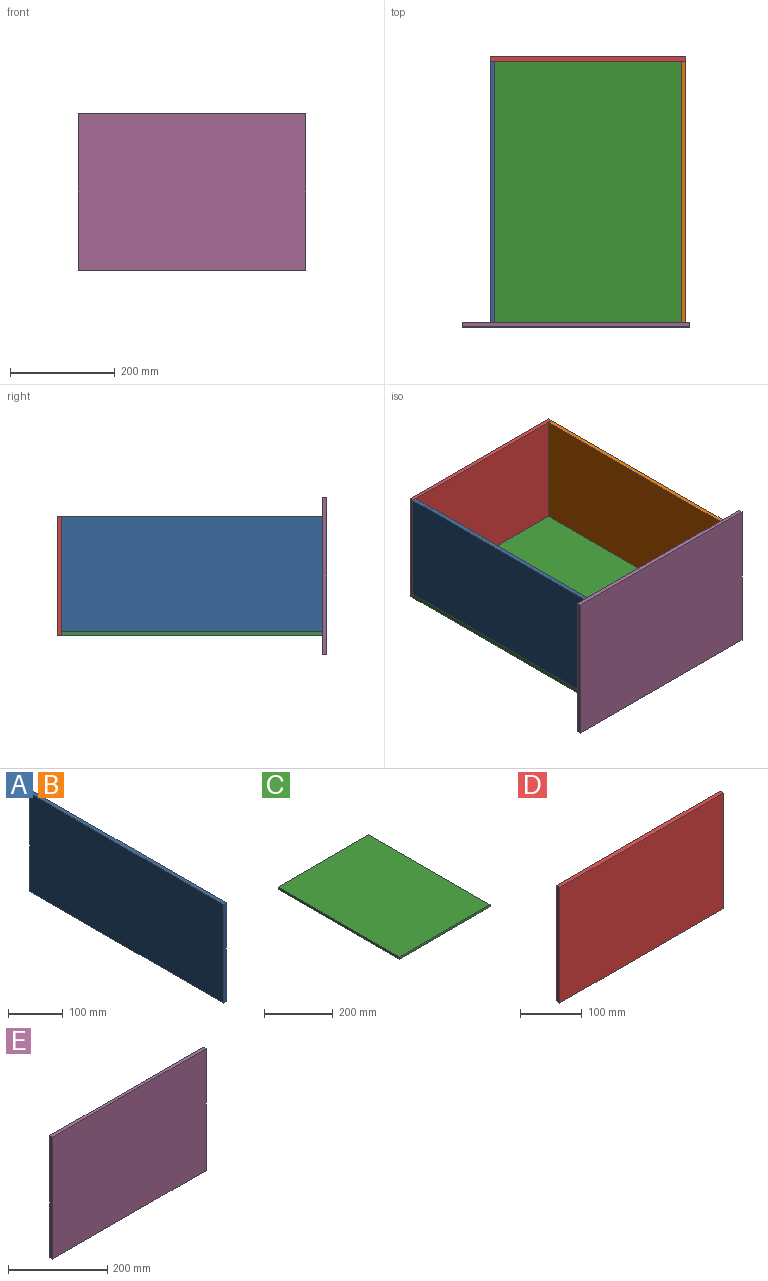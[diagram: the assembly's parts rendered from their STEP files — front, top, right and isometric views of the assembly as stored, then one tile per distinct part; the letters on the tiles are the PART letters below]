
ASSEMBLY  parts=5 mates=4
PART A: 6 faces, bbox 8x500x220 mm
  f0: plane 220x8mm, normal (0,1,0), area 1760mm2, adj f1,f3,f4,f5
  f1: plane 500x8mm, normal (0,0,1), area 4000mm2, adj f0,f2,f4,f5
  f2: plane 220x8mm, normal (0,-1,0), area 1760mm2, adj f1,f3,f4,f5
  f3: plane 500x8mm, normal (0,0,-1), area 4000mm2, adj f0,f2,f4,f5
  f4: plane 500x220mm, normal (1,0,0), area 110000mm2, adj f0,f1,f2,f3
  f5: plane 500x220mm, normal (-1,0,0), area 110000mm2, adj f0,f1,f2,f3
PART B: same geometry as A
PART C: 6 faces, bbox 374x500x8 mm
  f0: plane 500x8mm, normal (1,0,0), area 4000mm2, adj f1,f3,f4,f5
  f1: plane 374x8mm, normal (0,1,0), area 2992mm2, adj f0,f2,f4,f5
  f2: plane 500x8mm, normal (-1,0,0), area 4000mm2, adj f1,f3,f4,f5
  f3: plane 374x8mm, normal (0,-1,0), area 2992mm2, adj f0,f2,f4,f5
  f4: plane 500x374mm, normal (0,0,1), area 187000mm2, adj f0,f1,f2,f3
  f5: plane 500x374mm, normal (0,0,-1), area 187000mm2, adj f0,f1,f2,f3
PART D: 6 faces, bbox 374x8x228 mm
  f0: plane 228x8mm, normal (1,0,0), area 1824mm2, adj f1,f3,f4,f5
  f1: plane 374x8mm, normal (0,0,1), area 2992mm2, adj f0,f2,f4,f5
  f2: plane 228x8mm, normal (-1,0,0), area 1824mm2, adj f1,f3,f4,f5
  f3: plane 374x8mm, normal (0,0,-1), area 2992mm2, adj f0,f2,f4,f5
  f4: plane 374x228mm, normal (0,-1,0), area 85272mm2, adj f0,f1,f2,f3
  f5: plane 374x228mm, normal (0,1,0), area 85272mm2, adj f0,f1,f2,f3
PART E: 6 faces, bbox 436x8x300 mm
  f0: plane 300x8mm, normal (1,0,0), area 2400mm2, adj f1,f3,f4,f5
  f1: plane 436x8mm, normal (0,0,1), area 3488mm2, adj f0,f2,f4,f5
  f2: plane 300x8mm, normal (-1,0,0), area 2400mm2, adj f1,f3,f4,f5
  f3: plane 436x8mm, normal (0,0,-1), area 3488mm2, adj f0,f2,f4,f5
  f4: plane 436x300mm, normal (0,-1,0), area 130800mm2, adj f0,f1,f2,f3
  f5: plane 436x300mm, normal (0,1,0), area 130800mm2, adj f0,f1,f2,f3
PLACE A t=(-241.49,-0.94,160.31)mm
PLACE B t=(124.51,-0.94,160.31)mm
PLACE C t=(-54.49,-0.94,42.31)mm fixed
PLACE D t=(-54.49,257.06,156.31)mm
PLACE E t=(-77.49,-250.94,156.31)mm
MATE fastened D.f4 <-> B.f0  axis (0,-1,0) through (132.51,249.06,270.31)mm
MATE fastened B.f2 <-> C.f3  axis (0,-1,0) through (132.51,-250.94,50.31)mm
MATE fastened E.f5 <-> C.f3  axis (0,1,0) through (-295.49,-250.94,6.31)mm
MATE fastened A.f2 <-> C.f3  axis (0,-1,0) through (-241.49,-250.94,50.31)mm
